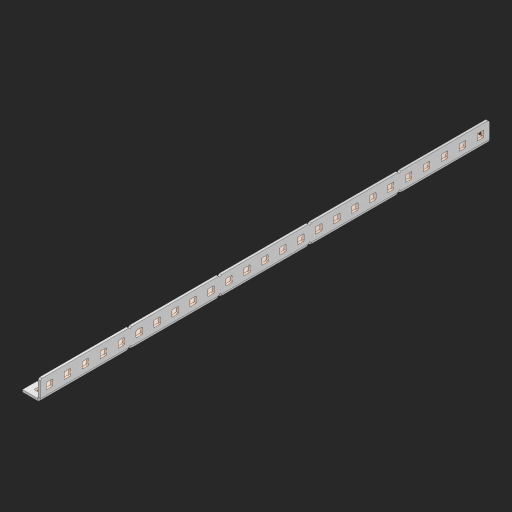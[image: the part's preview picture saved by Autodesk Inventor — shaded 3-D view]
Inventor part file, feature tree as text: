
AUTODESK INVENTOR PART (.ipt)
format: ipt  version: 2023 (Build 270158000, 158)  size: 1,105,408 bytes
history: native  units: in
note: dims shown in document units (in); Inventor stores cm internally (conversion verified against a paired STEP export)
features: other x223, extrude x73, sheet_metal_op x11, sketch x10, pattern_linear x2, mirror x1, chamfer x1
ambient origin geometry x8: Origin, YZ Plane, XZ Plane, XY Plane, X Axis, Y Axis, Z Axis, Center Point
bodies: Solid1 (feature_tree), Body (feature_tree)
feature tree (321):
  other  "Alu Half C 1x2x1x25"
  other  "Table"
  other  "Alu C 1x2x1x35"
  other  "Alu C 1x2x1x34"
  other  "Alu C 1x2x1x33"
  other  "Alu C 1x2x1x32"
  other  "Alu C 1x2x1x31"
  other  "Alu C 1x2x1x30"
  other  "Alu C 1x2x1x29"
  other  "Alu C 1x2x1x28"
  other  "Alu C 1x2x1x27"
  other  "Alu C 1x2x1x26"
  other  "Alu C 1x2x1x25"
  other  "Alu C 1x2x1x24"
  other  "Alu C 1x2x1x23"
  other  "Alu C 1x2x1x22"
  other  "Alu C 1x2x1x21"
  other  "Alu C 1x2x1x20"
  other  "Alu C 1x2x1x19"
  other  "Alu C 1x2x1x18"
  other  "Alu C 1x2x1x17"
  other  "Alu C 1x2x1x16"
  other  "Alu C 1x2x1x15"
  other  "Alu C 1x2x1x14"
  other  "Alu C 1x2x1x13"
  other  "Alu C 1x2x1x12"
  other  "Alu C 1x2x1x11"
  other  "Alu C 1x2x1x10"
  other  "Alu C 1x2x1x9"
  other  "Alu C 1x2x1x8"
  other  "Alu C 1x2x1x7"
  other  "Alu C 1x2x1x6"
  other  "Alu C 1x2x1x5"
  other  "Alu C 1x2x1x4"
  other  "Alu C 1x2x1x3"
  other  "Alu C 1x2x1x2"
  other  "Alu C 1x2x1x1"
  other  "Steel C 1x2x1x35"
  other  "Steel C 1x2x1x34"
  other  "Steel C 1x2x1x33"
  other  "Steel C 1x2x1x32"
  other  "Steel C 1x2x1x31"
  other  "Steel C 1x2x1x30"
  other  "Steel C 1x2x1x29"
  other  "Steel C 1x2x1x28"
  other  "Steel C 1x2x1x27"
  other  "Steel C 1x2x1x26"
  other  "Steel C 1x2x1x25"
  other  "Steel C 1x2x1x24"
  other  "Steel C 1x2x1x23"
  other  "Steel C 1x2x1x22"
  other  "Steel C 1x2x1x21"
  other  "Steel C 1x2x1x20"
  other  "Steel C 1x2x1x19"
  other  "Steel C 1x2x1x18"
  other  "Steel C 1x2x1x17"
  other  "Steel C 1x2x1x16"
  other  "Steel C 1x2x1x15"
  other  "Steel C 1x2x1x14"
  other  "Steel C 1x2x1x13"
  other  "Steel C 1x2x1x12"
  other  "Steel C 1x2x1x11"
  other  "Steel C 1x2x1x10"
  other  "Steel C 1x2x1x9"
  other  "Steel C 1x2x1x8"
  other  "Steel C 1x2x1x7"
  other  "Steel C 1x2x1x6"
  other  "Steel C 1x2x1x5"
  other  "Steel C 1x2x1x4"
  other  "Steel C 1x2x1x3"
  other  "Steel C 1x2x1x2"
  other  "Steel C 1x2x1x1"
  other  "Alu Half C 1x2x1x35"
  other  "Alu Half C 1x2x1x34"
  other  "Alu Half C 1x2x1x33"
  other  "Alu Half C 1x2x1x32"
  other  "Alu Half C 1x2x1x31"
  other  "Alu Half C 1x2x1x30"
  other  "Alu Half C 1x2x1x29"
  other  "Alu Half C 1x2x1x28"
  other  "Alu Half C 1x2x1x27"
  other  "Alu Half C 1x2x1x26"
  other  "Alu Half C 1x2x1x24"
  other  "Alu Half C 1x2x1x23"
  other  "Alu Half C 1x2x1x22"
  other  "Alu Half C 1x2x1x21"
  other  "Alu Half C 1x2x1x20"
  other  "Alu Half C 1x2x1x19"
  other  "Alu Half C 1x2x1x18"
  other  "Alu Half C 1x2x1x17"
  other  "Alu Half C 1x2x1x16"
  other  "Alu Half C 1x2x1x15"
  other  "Alu Half C 1x2x1x14"
  other  "Alu Half C 1x2x1x13"
  other  "Alu Half C 1x2x1x12"
  other  "Alu Half C 1x2x1x11"
  other  "Alu Half C 1x2x1x10"
  other  "Alu Half C 1x2x1x9"
  other  "Alu Half C 1x2x1x8"
  other  "Alu Half C 1x2x1x7"
  other  "Alu Half C 1x2x1x6"
  other  "Alu Half C 1x2x1x5"
  other  "Alu Half C 1x2x1x4"
  other  "Alu Half C 1x2x1x3"
  other  "Alu Half C 1x2x1x2"
  other  "Alu Half C 1x2x1x1"
  other  "Steel Half C 1x2x1x35"
  other  "Steel Half C 1x2x1x34"
  other  "Steel Half C 1x2x1x33"
  other  "Steel Half C 1x2x1x32"
  other  "Steel Half C 1x2x1x31"
  other  "Steel Half C 1x2x1x30"
  other  "Steel Half C 1x2x1x29"
  other  "Steel Half C 1x2x1x28"
  other  "Steel Half C 1x2x1x27"
  other  "Steel Half C 1x2x1x26"
  other  "Steel Half C 1x2x1x25"
  other  "Steel Half C 1x2x1x24"
  other  "Steel Half C 1x2x1x23"
  other  "Steel Half C 1x2x1x22"
  other  "Steel Half C 1x2x1x21"
  other  "Steel Half C 1x2x1x20"
  other  "Steel Half C 1x2x1x19"
  other  "Steel Half C 1x2x1x18"
  other  "Steel Half C 1x2x1x17"
  other  "Steel Half C 1x2x1x16"
  other  "Steel Half C 1x2x1x15"
  other  "Steel Half C 1x2x1x14"
  other  "Steel Half C 1x2x1x13"
  other  "Steel Half C 1x2x1x12"
  other  "Steel Half C 1x2x1x11"
  other  "Steel Half C 1x2x1x10"
  other  "Steel Half C 1x2x1x9"
  other  "Steel Half C 1x2x1x8"
  other  "Steel Half C 1x2x1x7"
  other  "Steel Half C 1x2x1x6"
  other  "Steel Half C 1x2x1x5"
  other  "Steel Half C 1x2x1x4"
  other  "Steel Half C 1x2x1x3"
  other  "Steel Half C 1x2x1x2"
  other  "Steel Half C 1x2x1x1"
  sheet_metal_op  "Flanges"
  other  "Flange Pattern Plane"
  other  "Flange Pattern Sketch"
  sheet_metal_op  "Flange Pattern"
  sheet_metal_op  "Body Pattern"
  pattern_linear  "Center Pattern"  Spacing1=0.0625in  [1 undecoded]
  other  "Arc Length"
  mirror  "Notch Mirror"
  pattern_linear  "Notch Pattern"  Spacing1=0.182in  [1 undecoded]
  chamfer  "End Chamfer"
  extrude  "Half Cut"  Depth=0.02in
  sketch  "Sketch1"  dims[d0=1.0in]
  other  "Plate1"
  sketch  "Sketch2"  dims[d1=12.5in]
  other  "Plate2"
  sheet_metal_op  "Bend1"
  sheet_metal_op  "Corner1"
  sketch  "Sketch3"  dims[d2=0.0625in]
  sketch  "Sketch7"  dims[d3=0.0625in]
  other  "Srf1"
  other  "Srf2"
  sketch  "Sketch8"  dims[d4=0.0312in]
  sketch  "Sketch9"  dims[d5=0.125in]
  other  "Srf91"
  sheet_metal_op  "Body Pattern Sketch"
  other  "Srf92"
  sketch  "Sketch13"  dims[d6=0.0625in]
  sketch  "Sketch14"  dims[d7=0.5in d8=90.0deg d9=0.0312in]
  sketch  "Sketch15"  dims[d10=0.25in]
  sketch  "Sketch16"  dims[d11=0.0625in d12=0.0625in d16=0.182in d17=0.02in d18=0.0625in d19=0.0in d20=0.25in d21=0.25in d38=9.8425in d40=0.5in d41=0.3937in d43=1.0in d46=0.172in d47=1.0in d48=0.0in d49=0.182in d50=0.02in d51=0.25in d52=0.25in d53=0.0625in d54=0.0in d55=0.172in d56=1.0in d57=0.0in d58=0.25in d60=9.8425in d62=0.5in d63=0.3937in d65=0.5in d85=0.1473in d86=0.1782in d88=0.04in d89=0.0625in d90=0.0in d91=0.04in d92=0.0491in d95=2.5in d96=0.04in d97=0.25in d98=45.0deg d99=0.25in d100=0.5in d101=0.0in d102=2.497in d106=0.182in d107=0.02in d108=0.5in d109=0.5in d110=0.0625in d111=0.0in d112=0.172in d113=0.5in d114=0.0in d117=0.5in d118=0.5in d119=0.5in]
  other  "Srf786"
  other  "Srf823"
  other  "Srf824"
  other  "Srf825"
  other  "Srf826"
  other  "Srf827"
  other  "Srf828"
  other  "Srf829"
  other  "Srf856"
  other  "Srf857"
  other  "Srf858"
  other  "Srf859"
  other  "Srf860"
  other  "Srf861"
  other  "Srf862"
  other  "Srf889"
  other  "Srf890"
  other  "Srf891"
  other  "Srf892"
  other  "Srf893"
  other  "Srf894"
  other  "Srf895"
  other  "Srf896"
  other  "Srf922"
  other  "Srf923"
  other  "Srf924"
  other  "Srf925"
  other  "Srf926"
  other  "Srf959"
  other  "Srf960"
  other  "Srf961"
  other  "Srf962"
  other  "Srf963"
  other  "Srf996"
  other  "Srf997"
  other  "Srf998"
  other  "Srf999"
  other  "Srf1000"
  other  "Srf1143"
  other  "Srf1144"
  other  "Srf1145"
  other  "Srf1146"
  other  "Srf1147"
  other  "Srf1148"
  other  "Srf1149"
  other  "Srf1150"
  other  "Srf1151"
  other  "Srf1152"
  other  "Srf1153"
  other  "Srf1199"
  other  "Srf1200"
  other  "Srf1201"
  other  "Srf1202"
  other  "Srf1203"
  other  "Srf1204"
  other  "Srf1205"
  other  "Srf1206"
  other  "Srf1207"
  other  "Srf1208"
  other  "Srf1209"
  other  "Srf1255"
  other  "Srf1256"
  other  "Srf1257"
  other  "Srf1258"
  other  "Srf1259"
  other  "Srf1260"
  other  "Srf1261"
  other  "Srf1262"
  other  "Srf1263"
  other  "Srf1264"
  other  "Srf1265"
  sheet_metal_op  "Flange Stamp"
  sheet_metal_op  "Flange Circle"
  sheet_metal_op  "Body Stamp"
  sheet_metal_op  "Body Circle"
  other  "Center Stamp"
  other  "Center Circle"
  sheet_metal_op  "Notch"
  extrude  "ExtrusionSrf2"  Depth=0.0625in
  extrude  "ExtrusionSrf92"  TaperAngle=0.0deg  [1 undecoded]
  extrude  "ExtrusionSrf823"  Depth=0.5in
  extrude  "ExtrusionSrf824"  Depth=0.5in
  extrude  "ExtrusionSrf825"  Depth=0.5in
  extrude  "ExtrusionSrf826"  Depth=0.5in
  extrude  "ExtrusionSrf827"  Depth=1.0in TaperAngle=0.0deg
  extrude  "ExtrusionSrf828"  Depth=0.182in
  extrude  "ExtrusionSrf829"  Depth=0.02in
  extrude  "ExtrusionSrf856"  Depth=0.5in
  extrude  "ExtrusionSrf857"  Depth=0.5in
  extrude  "ExtrusionSrf858"  Depth=0.0625in
  extrude  "ExtrusionSrf859"  TaperAngle=0.0deg  [1 undecoded]
  extrude  "ExtrusionSrf860"  Depth=0.5in
  extrude  "ExtrusionSrf861"  Depth=1.0in TaperAngle=0.0deg
  extrude  "ExtrusionSrf862"  Depth=0.5in
  extrude  "ExtrusionSrf889"  Depth=0.5in
  extrude  "ExtrusionSrf890"  Depth=0.5in
  extrude  "ExtrusionSrf891"  Depth=0.5in
  extrude  "ExtrusionSrf892"  Depth=0.5in
  extrude  "ExtrusionSrf893"  Depth=0.5in
  extrude  "ExtrusionSrf894"  Depth=0.0625in
  extrude  "ExtrusionSrf895"  TaperAngle=0.0deg  [1 undecoded]
  extrude  "ExtrusionSrf896"  Depth=0.5in
  extrude  "ExtrusionSrf922"  Depth=0.5in
  extrude  "ExtrusionSrf923"  Depth=0.5in
  extrude  "ExtrusionSrf924"  Depth=0.5in TaperAngle=45.0deg
  extrude  "ExtrusionSrf925"  Depth=0.5in
  extrude  "ExtrusionSrf926"  Depth=0.5in TaperAngle=0.0deg
  extrude  "ExtrusionSrf959"  Depth=0.5in
  extrude  "ExtrusionSrf960"  Depth=0.182in
  extrude  "ExtrusionSrf961"  Depth=0.02in
  extrude  "ExtrusionSrf962"  Depth=0.5in
  extrude  "ExtrusionSrf963"  Depth=0.5in
  extrude  "ExtrusionSrf996"  Depth=0.0625in
  extrude  "ExtrusionSrf997"  TaperAngle=0.0deg  [1 undecoded]
  extrude  "ExtrusionSrf998"  Depth=0.5in
  extrude  "ExtrusionSrf999"  Depth=0.5in TaperAngle=0.0deg
  extrude  "ExtrusionSrf1000"  Depth=0.5in
  extrude  "ExtrusionSrf1143"  Depth=0.5in
  extrude  "ExtrusionSrf1144"  Depth=0.5in
  extrude  "ExtrusionSrf1145"  [1 undecoded]
  extrude  "ExtrusionSrf1146"  [1 undecoded]
  extrude  "ExtrusionSrf1147"  [1 undecoded]
  extrude  "ExtrusionSrf1148"  [1 undecoded]
  extrude  "ExtrusionSrf1149"  [1 undecoded]
  extrude  "ExtrusionSrf1150"  [1 undecoded]
  extrude  "ExtrusionSrf1151"  [1 undecoded]
  extrude  "ExtrusionSrf1152"  [1 undecoded]
  extrude  "ExtrusionSrf1153"  [1 undecoded]
  extrude  "ExtrusionSrf1199"  [1 undecoded]
  extrude  "ExtrusionSrf1200"  [1 undecoded]
  extrude  "ExtrusionSrf1201"  [1 undecoded]
  extrude  "ExtrusionSrf1202"  [1 undecoded]
  extrude  "ExtrusionSrf1203"  [1 undecoded]
  extrude  "ExtrusionSrf1204"  [1 undecoded]
  extrude  "ExtrusionSrf1205"  [1 undecoded]
  extrude  "ExtrusionSrf1206"  [1 undecoded]
  extrude  "ExtrusionSrf1207"  [1 undecoded]
  extrude  "ExtrusionSrf1208"  [1 undecoded]
  extrude  "ExtrusionSrf1209"  [1 undecoded]
  extrude  "ExtrusionSrf1255"  [1 undecoded]
  extrude  "ExtrusionSrf1256"  [1 undecoded]
  extrude  "ExtrusionSrf1257"  [1 undecoded]
  extrude  "ExtrusionSrf1258"  [1 undecoded]
  extrude  "ExtrusionSrf1259"  [1 undecoded]
  extrude  "ExtrusionSrf1260"  [1 undecoded]
  extrude  "ExtrusionSrf1261"  [1 undecoded]
  extrude  "ExtrusionSrf1262"  [1 undecoded]
  extrude  "ExtrusionSrf1263"  [1 undecoded]
  extrude  "ExtrusionSrf1264"  [1 undecoded]
  extrude  "ExtrusionSrf1265"  [1 undecoded]
note: 37 required parameter values undecoded (feature->parameter linkage not recoverable at this tier; creation-order binding heuristic only, values carry confidence <= 0.55)
